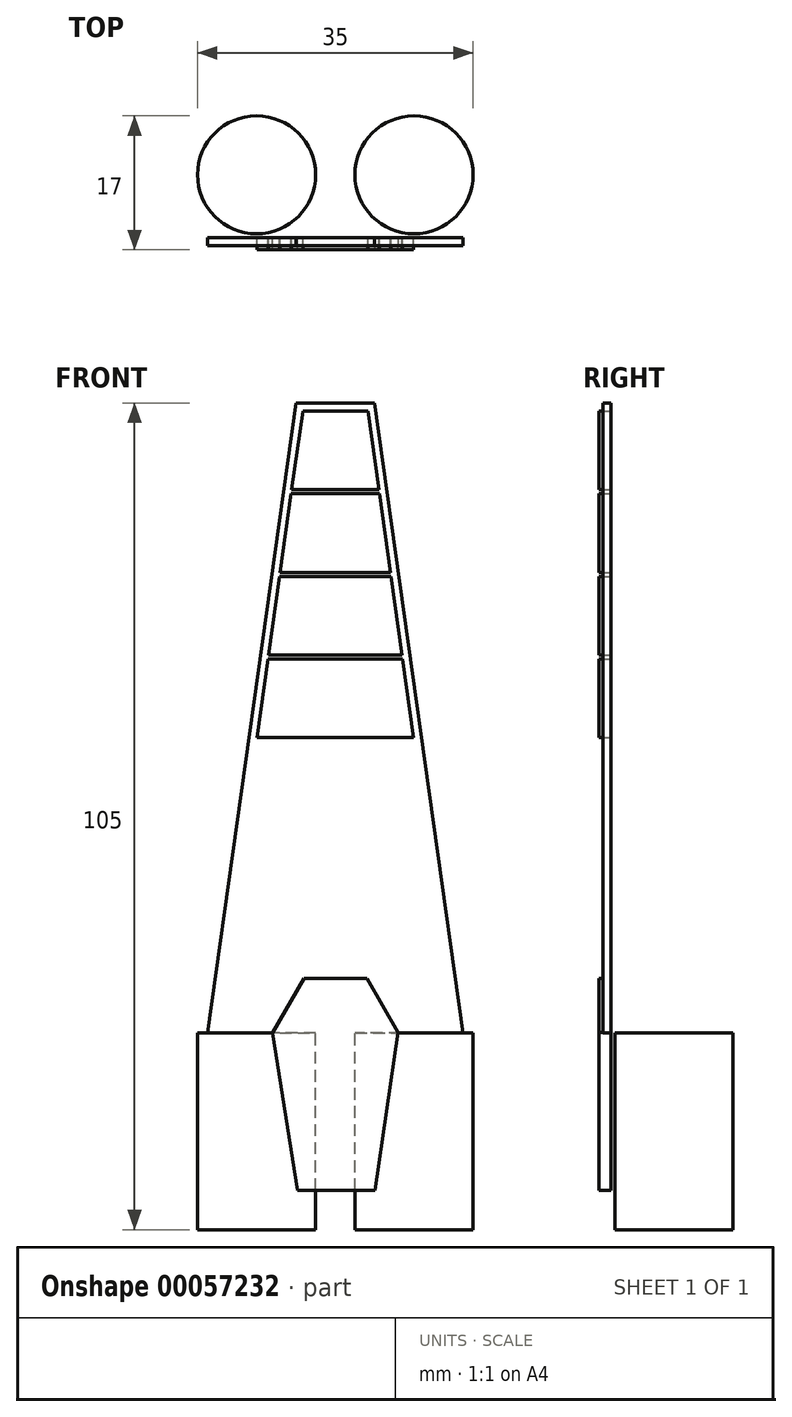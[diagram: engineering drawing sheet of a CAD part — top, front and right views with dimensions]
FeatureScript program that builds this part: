
annotation { "Feature Type Name" : "Feature", "Feature Type Description" : "" }
export const myFeature = defineFeature(function(context is Context, id is Id, definition is map)
    precondition{}
    {
        {
            var Q0;
            Q0=qCreatedBy(makeId("Front.planeOp"),FACE);
            var sketch = newSketch(context, id + "F0", { "sketchPlane" : qUnion([Q0])});
            skLineSegment(sketch, "E0", {"start": v(-5, 80) * mm, "end": v(-16.24, 0) * mm});
            skLineSegment(sketch, "E1.MirrorCS", {"start": v(5, 80) * mm, "end": v(16.24, 0) * mm});
            skLineSegment(sketch, "E2", {"start": v(-5, 80) * mm, "end": v(5, 80) * mm});
            skLineSegment(sketch, "E3", {"start": v(-16.24, 0) * mm, "end": v(16.24, 0) * mm});
            skSolve(sketch);
        }
        {
            var Q0;
            Q0=qCreatedBy(makeId("Front.planeOp"),FACE);
            var sketch = newSketch(context, id + "F1", { "sketchPlane" : qUnion([Q0])});
            skArc(sketch, "E4.cCircle", {"start": v(6, 3.46) * mm, "mid": v(0, 6.93) * mm, "end": v(-6, 3.46) * mm, "construction": true});
            skLineSegment(sketch, "E4.2", {"start": v(-8, 0) * mm, "end": v(-4, 6.93) * mm});
            skLineSegment(sketch, "E4.3", {"start": v(-4, 6.93) * mm, "end": v(4, 6.93) * mm});
            skLineSegment(sketch, "E4.4", {"start": v(4, 6.93) * mm, "end": v(7.98, 0.04) * mm});
            skPoint(sketch, "E4.0.midPoint", {"position": v(0, -6.93) * mm});
            skPoint(sketch, "E5.orphan", {"position": v(-4.16, -6.93) * mm});
            skPoint(sketch, "E6.orphan", {"position": v(4.16, -6.93) * mm});
            skLineSegment(sketch, "E7", {"start": v(-8, 0) * mm, "end": v(-4.8, -20) * mm});
            skLineSegment(sketch, "E8", {"start": v(-4.8, -20) * mm, "end": v(5.03, -20) * mm});
            skLineSegment(sketch, "E9", {"start": v(5.03, -20) * mm, "end": v(7.98, 0.04) * mm});
            skSolve(sketch);
        }
        {
            var Q0;
            Q0=qCreatedBy(makeId("Front.planeOp"),FACE);
            var sketch = newSketch(context, id + "F2", { "sketchPlane" : qUnion([Q0])});
            skLineSegment(sketch, "E10.0", {"start": v(4.13, 79) * mm, "end": v(-4.13, 79) * mm});
            skLineSegment(sketch, "E10.3", {"start": v(-4.13, 79) * mm, "end": v(-5.54, 69) * mm});
            skLineSegment(sketch, "E11", {"start": v(-5.54, 69) * mm, "end": v(5.54, 69) * mm});
            skLineSegment(sketch, "E12.0", {"start": v(-5.6, 68.5) * mm, "end": v(5.6, 68.5) * mm});
            skLineSegment(sketch, "E13.0", {"start": v(0.65, 75) * mm, "end": v(-0.65, 75) * mm});
            skLineSegment(sketch, "E14.0", {"start": v(0.65, 80) * mm, "end": v(-0.65, 80) * mm});
            skLineSegment(sketch, "E15.0", {"start": v(-10.5, 0) * mm, "end": v(10.5, 0) * mm});
            skLineSegment(sketch, "E16", {"start": v(-7.01, 58.5) * mm, "end": v(7.01, 58.5) * mm});
            skLineSegment(sketch, "E17", {"start": v(-8.49, 48) * mm, "end": v(8.49, 48) * mm});
            skLineSegment(sketch, "E18.0", {"start": v(-7.08, 58) * mm, "end": v(7.08, 58) * mm});
            skLineSegment(sketch, "E19", {"start": v(8.49, 48) * mm, "end": v(7.08, 58) * mm});
            skLineSegment(sketch, "E20", {"start": v(7.01, 58.5) * mm, "end": v(5.6, 68.5) * mm});
            skLineSegment(sketch, "E21", {"start": v(5.54, 69) * mm, "end": v(4.13, 79) * mm});
            skPoint(sketch, "E22.end.orphan", {"position": v(-16.3, 0) * mm});
            skLineSegment(sketch, "E23", {"start": v(-9.96, 37.5) * mm, "end": v(9.96, 37.5) * mm});
            skLineSegment(sketch, "E24.trimOffspring", {"start": v(8.56, 47.5) * mm, "end": v(9.96, 37.5) * mm});
            skLineSegment(sketch, "E25", {"start": v(-8.56, 47.5) * mm, "end": v(8.56, 47.5) * mm});
            skLineSegment(sketch, "E26.trimOffspring", {"start": v(-7.08, 58) * mm, "end": v(-8.49, 48) * mm});
            skLineSegment(sketch, "E27.trimOffspring", {"start": v(-8.56, 47.5) * mm, "end": v(-9.96, 37.5) * mm});
            skLineSegment(sketch, "E28.trimOffspring", {"start": v(-5.6, 68.5) * mm, "end": v(-7.01, 58.5) * mm});
            skSolve(sketch);
        }
        {
            var Q0;
            Q0 = qSketchRegion(id + "F2", true);
            extrude(context, id + "F3", {"entities" : qUnion([Q0]), "depth" : 1.5 * mm});
        }
        {
            var Q0;
            Q0 = qSketchRegion(id + "F0", true);
            extrude(context, id + "F4", {"entities" : qUnion([Q0]), "depth" : 1 * mm});
        }
        {
            var Q0;
            Q0 = qSketchRegion(id + "F1", true);
            extrude(context, id + "F5", {"entities" : qUnion([Q0]), "operationType" : NewBodyOperationType.ADD, "depth" : 1.5 * mm});
        }
        {
            var Q0;
            Q0=qCreatedBy(makeId("Top.planeOp"),FACE);
            var sketch = newSketch(context, id + "F6", { "sketchPlane" : qUnion([Q0])});
            skCircle(sketch, "E29", {"center": v(-10, 8) * mm, "radius": 7.5 * mm});
            skCircle(sketch, "E30.MirrorC", {"center": v(10, 8) * mm, "radius": 7.5 * mm});
            skSolve(sketch);
        }
        {
            var Q0;
            Q0 = qSketchRegion(id + "F6", true);
            extrude(context, id + "F7", {"entities" : qUnion([Q0]), "oppositeDirection" : true, "depth" : 25 * mm});
        }
    });
